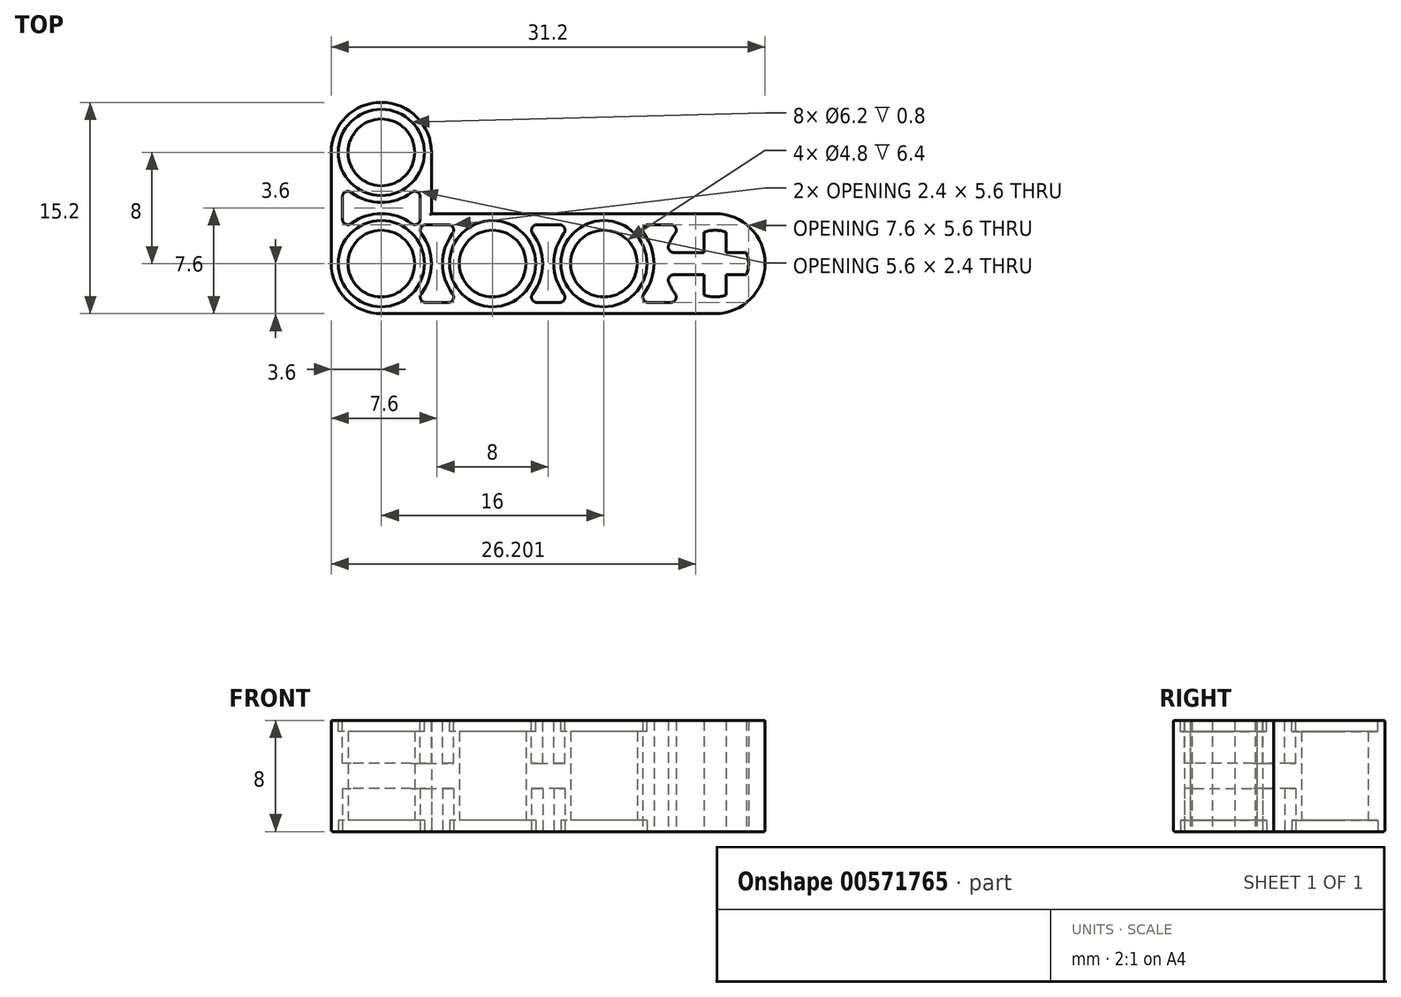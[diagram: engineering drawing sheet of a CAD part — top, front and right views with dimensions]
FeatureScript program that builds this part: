
annotation { "Feature Type Name" : "Feature", "Feature Type Description" : "" }
export const myFeature = defineFeature(function(context is Context, id is Id, definition is map)
    precondition{}
    {
        {
            var Q0;
            Q0=qCreatedBy(makeId("Top.planeOp"),FACE);
            var sketch = newSketch(context, id + "F0", { "sketchPlane" : qUnion([Q0])});
            skLineSegment(sketch, "E0", {"start": v(-13.78, 0) * mm, "end": v(26.94, 0) * mm, "construction": true});
            skCircle(sketch, "E1", {"center": v(0, 0) * mm, "radius": 3.1 * mm});
            skCircle(sketch, "E2", {"center": v(8, 0) * mm, "radius": 3.1 * mm});
            skCircle(sketch, "E3", {"center": v(16, 0) * mm, "radius": 3.1 * mm});
            skCircle(sketch, "E4", {"center": v(0, 8) * mm, "radius": 3.1 * mm});
            skLineSegment(sketch, "E5", {"start": v(24, 3.6) * mm, "end": v(24, -4.92) * mm, "construction": true});
            skArc(sketch, "E6", {"start": v(24, -3.6) * mm, "mid": v(27.6, 0) * mm, "end": v(24, 3.6) * mm});
            skArc(sketch, "E7", {"start": v(3.6, 8) * mm, "mid": v(0, 11.6) * mm, "end": v(-3.6, 8) * mm});
            skLineSegment(sketch, "E8", {"start": v(24, 3.6) * mm, "end": v(3.6, 3.6) * mm});
            skLineSegment(sketch, "E9", {"start": v(3.6, 3.6) * mm, "end": v(3.6, 8) * mm});
            skLineSegment(sketch, "E10", {"start": v(24, -3.6) * mm, "end": v(0, -3.6) * mm});
            skLineSegment(sketch, "E11", {"start": v(-3.6, 8) * mm, "end": v(-3.6, 0) * mm});
            skArc(sketch, "E12", {"start": v(-3.6, 0) * mm, "mid": v(-2.55, -2.55) * mm, "end": v(0, -3.6) * mm});
            skLineSegment(sketch, "E13", {"start": v(12, 5.04) * mm, "end": v(12, -3.98) * mm, "construction": true});
            skArc(sketch, "E14", {"start": v(10.88, -2.16) * mm, "mid": v(11.6, 0) * mm, "end": v(10.88, 2.16) * mm});
            skLineSegment(sketch, "E15", {"start": v(12, 2.8) * mm, "end": v(11.2, 2.8) * mm});
            skArc(sketch, "E16", {"start": v(11.2, 2.8) * mm, "mid": v(10.84, 2.58) * mm, "end": v(10.88, 2.16) * mm});
            skArc(sketch, "E17.MirrorCS", {"start": v(11.2, -2.8) * mm, "mid": v(10.84, -2.58) * mm, "end": v(10.88, -2.16) * mm});
            skLineSegment(sketch, "E18.MirrorCS", {"start": v(12, -2.8) * mm, "end": v(11.2, -2.8) * mm});
            skPoint(sketch, "E19.orphan", {"position": v(10.26, -2.8) * mm});
            skPoint(sketch, "E20.orphan", {"position": v(10.26, 2.8) * mm});
            skLineSegment(sketch, "E21.MirrorCS", {"start": v(12, 2.8) * mm, "end": v(12.8, 2.8) * mm});
            skArc(sketch, "E22.MirrorCS", {"start": v(12.8, 2.8) * mm, "mid": v(13.16, 2.58) * mm, "end": v(13.12, 2.16) * mm});
            skArc(sketch, "E23.MirrorCS", {"start": v(13.12, -2.16) * mm, "mid": v(12.4, 0) * mm, "end": v(13.12, 2.16) * mm});
            skArc(sketch, "E24.MirrorCS", {"start": v(12.8, -2.8) * mm, "mid": v(13.16, -2.58) * mm, "end": v(13.12, -2.16) * mm});
            skLineSegment(sketch, "E25.MirrorCS", {"start": v(12, -2.8) * mm, "end": v(12.8, -2.8) * mm});
            skLineSegment(sketch, "E26", {"start": v(16, 0) * mm, "end": v(16, 5.26) * mm, "construction": true});
            skLineSegment(sketch, "E27", {"start": v(8, 0) * mm, "end": v(8, 7.03) * mm, "construction": true});
            skLineSegment(sketch, "E28.MirrorCS", {"start": v(20, 2.8) * mm, "end": v(20.8, 2.8) * mm});
            skArc(sketch, "E29.MirrorCS", {"start": v(20.8, 2.8) * mm, "mid": v(21.16, 2.58) * mm, "end": v(21.12, 2.16) * mm});
            skArc(sketch, "E30.MirrorCS", {"start": v(21.12, -2.16) * mm, "mid": v(20.87, -1.77) * mm, "end": v(20.66, -1.35) * mm});
            skArc(sketch, "E31.MirrorCS", {"start": v(20.8, -2.8) * mm, "mid": v(21.16, -2.58) * mm, "end": v(21.12, -2.16) * mm});
            skLineSegment(sketch, "E32.MirrorCS", {"start": v(20, -2.8) * mm, "end": v(20.8, -2.8) * mm});
            skLineSegment(sketch, "E33.MirrorCS", {"start": v(20, -2.8) * mm, "end": v(19.2, -2.8) * mm});
            skArc(sketch, "E34.MirrorCS", {"start": v(19.2, -2.8) * mm, "mid": v(18.84, -2.58) * mm, "end": v(18.88, -2.16) * mm});
            skArc(sketch, "E35.MirrorCS", {"start": v(18.88, -2.16) * mm, "mid": v(19.6, 0) * mm, "end": v(18.88, 2.16) * mm});
            skArc(sketch, "E36.MirrorCS", {"start": v(19.2, 2.8) * mm, "mid": v(18.84, 2.58) * mm, "end": v(18.88, 2.16) * mm});
            skLineSegment(sketch, "E37.MirrorCS", {"start": v(20, 2.8) * mm, "end": v(19.2, 2.8) * mm});
            skLineSegment(sketch, "E38.MirrorCS", {"start": v(4, 2.8) * mm, "end": v(3.2, 2.8) * mm});
            skArc(sketch, "E39.MirrorCS", {"start": v(3.2, 2.8) * mm, "mid": v(2.84, 2.58) * mm, "end": v(2.88, 2.16) * mm});
            skArc(sketch, "E40.MirrorCS", {"start": v(2.88, -2.16) * mm, "mid": v(3.6, 0) * mm, "end": v(2.88, 2.16) * mm});
            skArc(sketch, "E41.MirrorCS", {"start": v(3.2, -2.8) * mm, "mid": v(2.84, -2.58) * mm, "end": v(2.88, -2.16) * mm});
            skLineSegment(sketch, "E42.MirrorCS", {"start": v(4, -2.8) * mm, "end": v(3.2, -2.8) * mm});
            skLineSegment(sketch, "E43.MirrorCS", {"start": v(4, -2.8) * mm, "end": v(4.8, -2.8) * mm});
            skArc(sketch, "E44.MirrorCS", {"start": v(4.8, -2.8) * mm, "mid": v(5.16, -2.58) * mm, "end": v(5.12, -2.16) * mm});
            skArc(sketch, "E45.MirrorCS", {"start": v(5.12, -2.16) * mm, "mid": v(4.4, 0) * mm, "end": v(5.12, 2.16) * mm});
            skArc(sketch, "E46.MirrorCS", {"start": v(4.8, 2.8) * mm, "mid": v(5.16, 2.58) * mm, "end": v(5.12, 2.16) * mm});
            skLineSegment(sketch, "E47.MirrorCS", {"start": v(4, 2.8) * mm, "end": v(4.8, 2.8) * mm});
            skArc(sketch, "E48", {"start": v(0, 3.6) * mm, "mid": v(-1.14, 3.42) * mm, "end": v(-2.16, 2.88) * mm});
            skLineSegment(sketch, "E49", {"start": v(-2.8, 4) * mm, "end": v(-2.8, 3.2) * mm});
            skArc(sketch, "E50", {"start": v(-2.8, 3.2) * mm, "mid": v(-2.58, 2.84) * mm, "end": v(-2.16, 2.88) * mm});
            skLineSegment(sketch, "E51", {"start": v(-4.22, 4) * mm, "end": v(5.13, 4) * mm, "construction": true});
            skArc(sketch, "E52.MirrorCS", {"start": v(0, 3.6) * mm, "mid": v(1.14, 3.42) * mm, "end": v(2.16, 2.88) * mm});
            skLineSegment(sketch, "E53.MirrorCS", {"start": v(2.8, 4) * mm, "end": v(2.8, 3.2) * mm});
            skArc(sketch, "E54.MirrorCS", {"start": v(2.8, 3.2) * mm, "mid": v(2.58, 2.84) * mm, "end": v(2.16, 2.88) * mm});
            skArc(sketch, "E55.MirrorCS", {"start": v(2.8, 4.8) * mm, "mid": v(2.58, 5.16) * mm, "end": v(2.16, 5.12) * mm});
            skArc(sketch, "E56.MirrorCS", {"start": v(0, 4.4) * mm, "mid": v(-1.14, 4.58) * mm, "end": v(-2.16, 5.12) * mm});
            skArc(sketch, "E57.MirrorCS", {"start": v(-2.8, 4.8) * mm, "mid": v(-2.58, 5.16) * mm, "end": v(-2.16, 5.12) * mm});
            skLineSegment(sketch, "E58.MirrorCS", {"start": v(2.8, 4) * mm, "end": v(2.8, 4.8) * mm});
            skLineSegment(sketch, "E59.MirrorCS", {"start": v(-2.8, 4) * mm, "end": v(-2.8, 4.8) * mm});
            skArc(sketch, "E60.MirrorCS", {"start": v(0, 4.4) * mm, "mid": v(1.14, 4.58) * mm, "end": v(2.16, 5.12) * mm});
            skLineSegment(sketch, "E61", {"start": v(21.03, 0.8) * mm, "end": v(23.2, 0.8) * mm});
            skLineSegment(sketch, "E62", {"start": v(23.2, 2.26) * mm, "end": v(23.2, 0.8) * mm});
            skArc(sketch, "E63", {"start": v(20.66, 1.35) * mm, "mid": v(20.7, 0.98) * mm, "end": v(21.03, 0.8) * mm});
            skLineSegment(sketch, "E64.MirrorCS", {"start": v(24.8, 2.26) * mm, "end": v(24.8, 0.8) * mm});
            skArc(sketch, "E65.MirrorCS", {"start": v(20.66, -1.35) * mm, "mid": v(20.7, -0.98) * mm, "end": v(21.03, -0.8) * mm});
            skLineSegment(sketch, "E66.MirrorCS", {"start": v(21.03, -0.8) * mm, "end": v(23.2, -0.8) * mm});
            skLineSegment(sketch, "E67.trimOffspring", {"start": v(24.8, 0.8) * mm, "end": v(26.26, 0.8) * mm});
            skLineSegment(sketch, "E68.trimOffspring", {"start": v(24.8, -0.8) * mm, "end": v(26.26, -0.8) * mm});
            skLineSegment(sketch, "E69.trimOffspring", {"start": v(24.8, -0.8) * mm, "end": v(24.8, -2.26) * mm});
            skLineSegment(sketch, "E70.trimOffspring", {"start": v(23.2, -0.8) * mm, "end": v(23.2, -2.26) * mm});
            skArc(sketch, "E71.trimOffspring", {"start": v(20.66, 1.35) * mm, "mid": v(20.87, 1.77) * mm, "end": v(21.12, 2.16) * mm});
            skPoint(sketch, "E72.orphan", {"position": v(20.5, 0.8) * mm});
            skPoint(sketch, "E73.orphan", {"position": v(20.5, -0.8) * mm});
            skArc(sketch, "E74", {"start": v(23.2, 2.26) * mm, "mid": v(24, 2.4) * mm, "end": v(24.8, 2.26) * mm});
            skArc(sketch, "E75", {"start": v(23.2, -2.26) * mm, "mid": v(24, -2.4) * mm, "end": v(24.8, -2.26) * mm});
            skArc(sketch, "E76", {"start": v(26.26, 0.8) * mm, "mid": v(26.4, 0) * mm, "end": v(26.26, -0.8) * mm});
            skCircle(sketch, "E77", {"center": v(0, 0) * mm, "radius": 2.4 * mm});
            skCircle(sketch, "E78", {"center": v(8, 0) * mm, "radius": 2.4 * mm});
            skCircle(sketch, "E79", {"center": v(16, 0) * mm, "radius": 2.4 * mm});
            skCircle(sketch, "E80", {"center": v(0, 8) * mm, "radius": 2.4 * mm});
            skSolve(sketch);
        }
        {
            var Q0;
            Q0=qCreatedBy(makeId("Top.planeOp"),FACE);
            var sketch = newSketch(context, id + "F1", { "sketchPlane" : qUnion([Q0])});
            skLineSegment(sketch, "E81.0", {"start": v(-3.6, 8) * mm, "end": v(-3.6, 0) * mm});
            skArc(sketch, "E82.0", {"start": v(3.6, 8) * mm, "mid": v(0, 11.6) * mm, "end": v(-3.6, 8) * mm});
            skLineSegment(sketch, "E83.0", {"start": v(3.6, 3.6) * mm, "end": v(3.6, 8) * mm});
            skLineSegment(sketch, "E84.0", {"start": v(24, 3.6) * mm, "end": v(3.6, 3.6) * mm});
            skArc(sketch, "E85.0", {"start": v(24, -3.6) * mm, "mid": v(27.6, 0) * mm, "end": v(24, 3.6) * mm});
            skLineSegment(sketch, "E86.0", {"start": v(24, -3.6) * mm, "end": v(0, -3.6) * mm});
            skArc(sketch, "E87.0", {"start": v(-3.6, 0) * mm, "mid": v(-2.55, -2.55) * mm, "end": v(0, -3.6) * mm});
            skSolve(sketch);
        }
        {
            var Q0;
            Q0=makeQuery(id+"F1.imprint","IMPRINT",FACE,{"disambiguationData":[TD([[makeQuery(id+"F1.imprint","IMPRINT",EDGE,{"derivedFrom":sQuery(id+"F1.wireOp",EDGE,"E81.0")}),1.0]])]});
            extrude(context, id + "F2", {"entities" : qUnion([Q0]), "depth" : 8 * mm, "offsetDistance" : 25 * mm});
        }
        {
            var Q0;
            Q0=makeQuery(id+"F0.imprint","IMPRINT",FACE,{"disambiguationData":[TD([[makeQuery(id+"F0.imprint","IMPRINT",EDGE,{"derivedFrom":sQuery(id+"F0.wireOp",EDGE,"E28.MirrorCS")}),-1.0]])]});
            extrude(context, id + "F3", {"entities" : qUnion([Q0]), "operationType" : NewBodyOperationType.REMOVE, "endBound" : BoundingType.THROUGH_ALL, "depth" : 25 * mm, "offsetDistance" : 25 * mm});
        }
        {
            var Q0;
            Q0=makeQuery(id+"F0.imprint","IMPRINT",FACE,{"disambiguationData":[TD([[makeQuery(id+"F0.imprint","IMPRINT",EDGE,{"derivedFrom":sQuery(id+"F0.wireOp",EDGE,"E1")}),-1.0]])]});
            var sketch = newSketch(context, id + "F4", { "sketchPlane" : qUnion([Q0])});
            skCircle(sketch, "E88.0", {"center": v(16, 0) * mm, "radius": 2.4 * mm});
            skCircle(sketch, "E89.0", {"center": v(8, 0) * mm, "radius": 2.4 * mm});
            skCircle(sketch, "E90.0", {"center": v(0, 0) * mm, "radius": 2.4 * mm});
            skCircle(sketch, "E91.0", {"center": v(0, 8) * mm, "radius": 2.4 * mm});
            skSolve(sketch);
        }
        {
            var Q0;
            Q0 = qSketchRegion(id + "F4", true);
            extrude(context, id + "F5", {"entities" : qUnion([Q0]), "operationType" : NewBodyOperationType.REMOVE, "endBound" : BoundingType.THROUGH_ALL, "depth" : 25 * mm, "offsetDistance" : 25 * mm});
        }
        {
            var Q0;
            Q0=makeQuery(id+"F0.imprint","IMPRINT",FACE,{"disambiguationData":[TD([[makeQuery(id+"F0.imprint","IMPRINT",EDGE,{"derivedFrom":sQuery(id+"F0.wireOp",EDGE,"E1")}),-1.0]])]});
            var sketch = newSketch(context, id + "F6", { "sketchPlane" : qUnion([Q0])});
            skCircle(sketch, "E92.0", {"center": v(16, 0) * mm, "radius": 3.1 * mm});
            skCircle(sketch, "E93.0", {"center": v(8, 0) * mm, "radius": 3.1 * mm});
            skCircle(sketch, "E94.0", {"center": v(0, 0) * mm, "radius": 3.1 * mm});
            skCircle(sketch, "E95.0", {"center": v(0, 8) * mm, "radius": 3.1 * mm});
            skSolve(sketch);
        }
        {
            var Q0;
            Q0 = qSketchRegion(id + "F6", true);
            extrude(context, id + "F7", {"entities" : qUnion([Q0]), "operationType" : NewBodyOperationType.REMOVE, "depth" : 0.8 * mm, "offsetDistance" : 25 * mm});
        }
        {
            var Q0;
            Q0=makeQuery(id+"F2.opExtrude","CAP_FACE",FACE,{"disambiguationData":[OSD([sQuery(id+"F1.wireOp",EDGE,"E81.0"),sQuery(id+"F1.wireOp",EDGE,"E82.0"),sQuery(id+"F1.wireOp",EDGE,"E83.0"),sQuery(id+"F1.wireOp",EDGE,"E84.0"),sQuery(id+"F1.wireOp",EDGE,"E85.0"),sQuery(id+"F1.wireOp",EDGE,"E86.0"),sQuery(id+"F1.wireOp",EDGE,"E87.0")])],"isStart":false});
            var sketch = newSketch(context, id + "F8", { "sketchPlane" : qUnion([Q0])});
            skCircle(sketch, "E96.0", {"center": v(0, 0) * mm, "radius": 3.1 * mm});
            skCircle(sketch, "E97.0", {"center": v(0, 8) * mm, "radius": 3.1 * mm});
            skCircle(sketch, "E98.0", {"center": v(8, 0) * mm, "radius": 3.1 * mm});
            skCircle(sketch, "E99.0", {"center": v(16, 0) * mm, "radius": 3.1 * mm});
            skSolve(sketch);
        }
        {
            var Q0;
            Q0 = qSketchRegion(id + "F8", true);
            extrude(context, id + "F9", {"entities" : qUnion([Q0]), "operationType" : NewBodyOperationType.REMOVE, "oppositeDirection" : true, "depth" : 0.8 * mm, "offsetDistance" : 25 * mm});
        }
        {
            var Q0;
            Q0=makeQuery(id+"F2.opExtrude","CAP_EDGE",EDGE,{"disambiguationData":[OSD([sQuery(id+"F1.wireOp",EDGE,"E82.0")])],"isStart":false});
            var Q1;
            Q1=makeQuery(id+"F2.opExtrude","CAP_EDGE",EDGE,{"disambiguationData":[OSD([sQuery(id+"F1.wireOp",EDGE,"E83.0")])],"isStart":false});
            var Q2;
            Q2=makeQuery(id+"F2.opExtrude","CAP_EDGE",EDGE,{"disambiguationData":[OSD([sQuery(id+"F1.wireOp",EDGE,"E84.0")])],"isStart":false});
            var Q3;
            Q3=makeQuery(id+"F2.opExtrude","CAP_EDGE",EDGE,{"disambiguationData":[OSD([sQuery(id+"F1.wireOp",EDGE,"E85.0")])],"isStart":false});
            var Q4;
            Q4=makeQuery(id+"F2.opExtrude","CAP_EDGE",EDGE,{"disambiguationData":[OSD([sQuery(id+"F1.wireOp",EDGE,"E86.0")])],"isStart":false});
            var Q5;
            Q5=makeQuery(id+"F2.opExtrude","CAP_EDGE",EDGE,{"disambiguationData":[OSD([sQuery(id+"F1.wireOp",EDGE,"E87.0")])],"isStart":false});
            var Q6;
            Q6=makeQuery(id+"F2.opExtrude","CAP_EDGE",EDGE,{"disambiguationData":[OSD([sQuery(id+"F1.wireOp",EDGE,"E81.0")])],"isStart":false});
            fillet(context, id + "F10", {"entities" : qUnion([Q0, Q1, Q2, Q3, Q4, Q5, Q6]), "radius" : 0.1 * mm, "tangentPropagation" : true, "allowEdgeOverflow" : false});
        }
        {
            var Q0;
            Q0=makeQuery(id+"F2.opExtrude","CAP_EDGE",EDGE,{"disambiguationData":[OSD([sQuery(id+"F1.wireOp",EDGE,"E86.0")])],"isStart":true});
            var Q1;
            Q1=makeQuery(id+"F2.opExtrude","CAP_EDGE",EDGE,{"disambiguationData":[OSD([sQuery(id+"F1.wireOp",EDGE,"E85.0")])],"isStart":true});
            var Q2;
            Q2=makeQuery(id+"F2.opExtrude","CAP_EDGE",EDGE,{"disambiguationData":[OSD([sQuery(id+"F1.wireOp",EDGE,"E84.0")])],"isStart":true});
            var Q3;
            Q3=makeQuery(id+"F2.opExtrude","CAP_EDGE",EDGE,{"disambiguationData":[OSD([sQuery(id+"F1.wireOp",EDGE,"E83.0")])],"isStart":true});
            var Q4;
            Q4=makeQuery(id+"F2.opExtrude","CAP_EDGE",EDGE,{"disambiguationData":[OSD([sQuery(id+"F1.wireOp",EDGE,"E82.0")])],"isStart":true});
            var Q5;
            Q5=makeQuery(id+"F2.opExtrude","CAP_EDGE",EDGE,{"disambiguationData":[OSD([sQuery(id+"F1.wireOp",EDGE,"E81.0")])],"isStart":true});
            var Q6;
            Q6=makeQuery(id+"F2.opExtrude","CAP_EDGE",EDGE,{"disambiguationData":[OSD([sQuery(id+"F1.wireOp",EDGE,"E87.0")])],"isStart":true});
            fillet(context, id + "F11", {"entities" : qUnion([Q0, Q1, Q2, Q3, Q4, Q5, Q6]), "radius" : 0.1 * mm, "tangentPropagation" : true, "allowEdgeOverflow" : false});
        }
        {
            var Q0;
            Q0=makeQuery(id+"F0.imprint","IMPRINT",FACE,{"disambiguationData":[TD([[makeQuery(id+"F0.imprint","IMPRINT",EDGE,{"derivedFrom":sQuery(id+"F0.wireOp",EDGE,"E1")}),-1.0]])]});
            var sketch = newSketch(context, id + "F12", { "sketchPlane" : qUnion([Q0])});
            skArc(sketch, "E100.0", {"start": v(4.8, -2.8) * mm, "mid": v(5.16, -2.58) * mm, "end": v(5.12, -2.16) * mm});
            skArc(sketch, "E100.1", {"start": v(3.2, 2.8) * mm, "mid": v(2.84, 2.58) * mm, "end": v(2.88, 2.16) * mm});
            skLineSegment(sketch, "E100.2", {"start": v(4, -2.8) * mm, "end": v(3.2, -2.8) * mm});
            skArc(sketch, "E100.3", {"start": v(4.8, 2.8) * mm, "mid": v(5.16, 2.58) * mm, "end": v(5.12, 2.16) * mm});
            skLineSegment(sketch, "E100.4", {"start": v(4, 2.8) * mm, "end": v(3.2, 2.8) * mm});
            skLineSegment(sketch, "E100.5", {"start": v(4, 2.8) * mm, "end": v(4.8, 2.8) * mm});
            skArc(sketch, "E100.6", {"start": v(5.12, -2.16) * mm, "mid": v(4.4, 0) * mm, "end": v(5.12, 2.16) * mm});
            skArc(sketch, "E100.7", {"start": v(3.2, -2.8) * mm, "mid": v(2.84, -2.58) * mm, "end": v(2.88, -2.16) * mm});
            skLineSegment(sketch, "E100.8", {"start": v(4, -2.8) * mm, "end": v(4.8, -2.8) * mm});
            skArc(sketch, "E100.9", {"start": v(2.88, -2.16) * mm, "mid": v(3.6, 0) * mm, "end": v(2.88, 2.16) * mm});
            skLineSegment(sketch, "E101.0", {"start": v(2.8, 4) * mm, "end": v(2.8, 4.8) * mm});
            skArc(sketch, "E101.1", {"start": v(0, 3.6) * mm, "mid": v(-1.14, 3.42) * mm, "end": v(-2.16, 2.88) * mm});
            skArc(sketch, "E101.2", {"start": v(2.8, 4.8) * mm, "mid": v(2.58, 5.16) * mm, "end": v(2.16, 5.12) * mm});
            skArc(sketch, "E101.3", {"start": v(-2.8, 3.2) * mm, "mid": v(-2.58, 2.84) * mm, "end": v(-2.16, 2.88) * mm});
            skArc(sketch, "E101.4", {"start": v(0, 4.4) * mm, "mid": v(1.14, 4.58) * mm, "end": v(2.16, 5.12) * mm});
            skArc(sketch, "E101.5", {"start": v(-2.8, 4.8) * mm, "mid": v(-2.58, 5.16) * mm, "end": v(-2.16, 5.12) * mm});
            skLineSegment(sketch, "E101.6", {"start": v(2.8, 4) * mm, "end": v(2.8, 3.2) * mm});
            skArc(sketch, "E101.7", {"start": v(2.8, 3.2) * mm, "mid": v(2.58, 2.84) * mm, "end": v(2.16, 2.88) * mm});
            skLineSegment(sketch, "E101.8", {"start": v(-2.8, 4) * mm, "end": v(-2.8, 4.8) * mm});
            skLineSegment(sketch, "E101.9", {"start": v(-2.8, 4) * mm, "end": v(-2.8, 3.2) * mm});
            skArc(sketch, "E101.10", {"start": v(0, 4.4) * mm, "mid": v(-1.14, 4.58) * mm, "end": v(-2.16, 5.12) * mm});
            skArc(sketch, "E101.11", {"start": v(0, 3.6) * mm, "mid": v(1.14, 3.42) * mm, "end": v(2.16, 2.88) * mm});
            skArc(sketch, "E102.0", {"start": v(11.2, -2.8) * mm, "mid": v(10.84, -2.58) * mm, "end": v(10.88, -2.16) * mm});
            skArc(sketch, "E102.1", {"start": v(13.12, -2.16) * mm, "mid": v(12.4, 0) * mm, "end": v(13.12, 2.16) * mm});
            skArc(sketch, "E102.2", {"start": v(11.2, 2.8) * mm, "mid": v(10.84, 2.58) * mm, "end": v(10.88, 2.16) * mm});
            skArc(sketch, "E102.3", {"start": v(12.8, 2.8) * mm, "mid": v(13.16, 2.58) * mm, "end": v(13.12, 2.16) * mm});
            skLineSegment(sketch, "E102.4", {"start": v(12, -2.8) * mm, "end": v(12.8, -2.8) * mm});
            skLineSegment(sketch, "E102.5", {"start": v(12, 2.8) * mm, "end": v(11.2, 2.8) * mm});
            skArc(sketch, "E102.6", {"start": v(10.88, -2.16) * mm, "mid": v(11.6, 0) * mm, "end": v(10.88, 2.16) * mm});
            skLineSegment(sketch, "E102.7", {"start": v(12, 2.8) * mm, "end": v(12.8, 2.8) * mm});
            skArc(sketch, "E102.8", {"start": v(12.8, -2.8) * mm, "mid": v(13.16, -2.58) * mm, "end": v(13.12, -2.16) * mm});
            skLineSegment(sketch, "E102.9", {"start": v(12, -2.8) * mm, "end": v(11.2, -2.8) * mm});
            skSolve(sketch);
        }
        {
            var Q0;
            Q0 = qSketchRegion(id + "F12", true);
            extrude(context, id + "F13", {"entities" : qUnion([Q0]), "operationType" : NewBodyOperationType.REMOVE, "depth" : 3.1 * mm, "offsetDistance" : 25 * mm});
        }
        {
            var Q0;
            Q0=makeQuery(id+"F2.opExtrude","CAP_FACE",FACE,{"disambiguationData":[OSD([sQuery(id+"F1.wireOp",EDGE,"E81.0"),sQuery(id+"F1.wireOp",EDGE,"E82.0"),sQuery(id+"F1.wireOp",EDGE,"E83.0"),sQuery(id+"F1.wireOp",EDGE,"E84.0"),sQuery(id+"F1.wireOp",EDGE,"E85.0"),sQuery(id+"F1.wireOp",EDGE,"E86.0"),sQuery(id+"F1.wireOp",EDGE,"E87.0")])],"isStart":false});
            var sketch = newSketch(context, id + "F14", { "sketchPlane" : qUnion([Q0])});
            skArc(sketch, "E103.0", {"start": v(11.2, -2.8) * mm, "mid": v(10.84, -2.58) * mm, "end": v(10.88, -2.16) * mm});
            skArc(sketch, "E103.1", {"start": v(13.12, -2.16) * mm, "mid": v(12.4, 0) * mm, "end": v(13.12, 2.16) * mm});
            skArc(sketch, "E103.2", {"start": v(11.2, 2.8) * mm, "mid": v(10.84, 2.58) * mm, "end": v(10.88, 2.16) * mm});
            skArc(sketch, "E103.3", {"start": v(12.8, 2.8) * mm, "mid": v(13.16, 2.58) * mm, "end": v(13.12, 2.16) * mm});
            skLineSegment(sketch, "E103.4", {"start": v(12, -2.8) * mm, "end": v(12.8, -2.8) * mm});
            skLineSegment(sketch, "E103.5", {"start": v(12, 2.8) * mm, "end": v(11.2, 2.8) * mm});
            skArc(sketch, "E103.6", {"start": v(10.88, -2.16) * mm, "mid": v(11.6, 0) * mm, "end": v(10.88, 2.16) * mm});
            skLineSegment(sketch, "E103.7", {"start": v(12, 2.8) * mm, "end": v(12.8, 2.8) * mm});
            skArc(sketch, "E103.8", {"start": v(12.8, -2.8) * mm, "mid": v(13.16, -2.58) * mm, "end": v(13.12, -2.16) * mm});
            skLineSegment(sketch, "E103.9", {"start": v(12, -2.8) * mm, "end": v(11.2, -2.8) * mm});
            skArc(sketch, "E104.0", {"start": v(4.8, -2.8) * mm, "mid": v(5.16, -2.58) * mm, "end": v(5.12, -2.16) * mm});
            skArc(sketch, "E104.1", {"start": v(3.2, 2.8) * mm, "mid": v(2.84, 2.58) * mm, "end": v(2.88, 2.16) * mm});
            skLineSegment(sketch, "E104.2", {"start": v(4, -2.8) * mm, "end": v(3.2, -2.8) * mm});
            skArc(sketch, "E104.3", {"start": v(4.8, 2.8) * mm, "mid": v(5.16, 2.58) * mm, "end": v(5.12, 2.16) * mm});
            skLineSegment(sketch, "E104.4", {"start": v(4, 2.8) * mm, "end": v(3.2, 2.8) * mm});
            skLineSegment(sketch, "E104.5", {"start": v(4, 2.8) * mm, "end": v(4.8, 2.8) * mm});
            skArc(sketch, "E104.6", {"start": v(5.12, -2.16) * mm, "mid": v(4.4, 0) * mm, "end": v(5.12, 2.16) * mm});
            skArc(sketch, "E104.7", {"start": v(3.2, -2.8) * mm, "mid": v(2.84, -2.58) * mm, "end": v(2.88, -2.16) * mm});
            skLineSegment(sketch, "E104.8", {"start": v(4, -2.8) * mm, "end": v(4.8, -2.8) * mm});
            skArc(sketch, "E104.9", {"start": v(2.88, -2.16) * mm, "mid": v(3.6, 0) * mm, "end": v(2.88, 2.16) * mm});
            skArc(sketch, "E105.0", {"start": v(0, 3.6) * mm, "mid": v(1.14, 3.42) * mm, "end": v(2.16, 2.88) * mm});
            skArc(sketch, "E106.0", {"start": v(0, 3.6) * mm, "mid": v(-1.14, 3.42) * mm, "end": v(-2.16, 2.88) * mm});
            skArc(sketch, "E107.0", {"start": v(-2.8, 3.2) * mm, "mid": v(-2.58, 2.84) * mm, "end": v(-2.16, 2.88) * mm});
            skLineSegment(sketch, "E108.0", {"start": v(-2.8, 4) * mm, "end": v(-2.8, 3.2) * mm});
            skLineSegment(sketch, "E109.0", {"start": v(-2.8, 4) * mm, "end": v(-2.8, 4.8) * mm});
            skArc(sketch, "E110.0", {"start": v(-2.8, 4.8) * mm, "mid": v(-2.58, 5.16) * mm, "end": v(-2.16, 5.12) * mm});
            skArc(sketch, "E111.0", {"start": v(0, 4.4) * mm, "mid": v(-1.14, 4.58) * mm, "end": v(-2.16, 5.12) * mm});
            skArc(sketch, "E112.0", {"start": v(0, 4.4) * mm, "mid": v(1.14, 4.58) * mm, "end": v(2.16, 5.12) * mm});
            skArc(sketch, "E113.0", {"start": v(2.8, 4.8) * mm, "mid": v(2.58, 5.16) * mm, "end": v(2.16, 5.12) * mm});
            skLineSegment(sketch, "E114.0", {"start": v(2.8, 4) * mm, "end": v(2.8, 4.8) * mm});
            skLineSegment(sketch, "E115.0", {"start": v(2.8, 4) * mm, "end": v(2.8, 3.2) * mm});
            skArc(sketch, "E116.0", {"start": v(2.8, 3.2) * mm, "mid": v(2.58, 2.84) * mm, "end": v(2.16, 2.88) * mm});
            skSolve(sketch);
        }
        {
            var Q0;
            Q0 = qSketchRegion(id + "F14", true);
            extrude(context, id + "F15", {"entities" : qUnion([Q0]), "operationType" : NewBodyOperationType.REMOVE, "oppositeDirection" : true, "depth" : 3.1 * mm, "offsetDistance" : 25 * mm});
        }
    });
